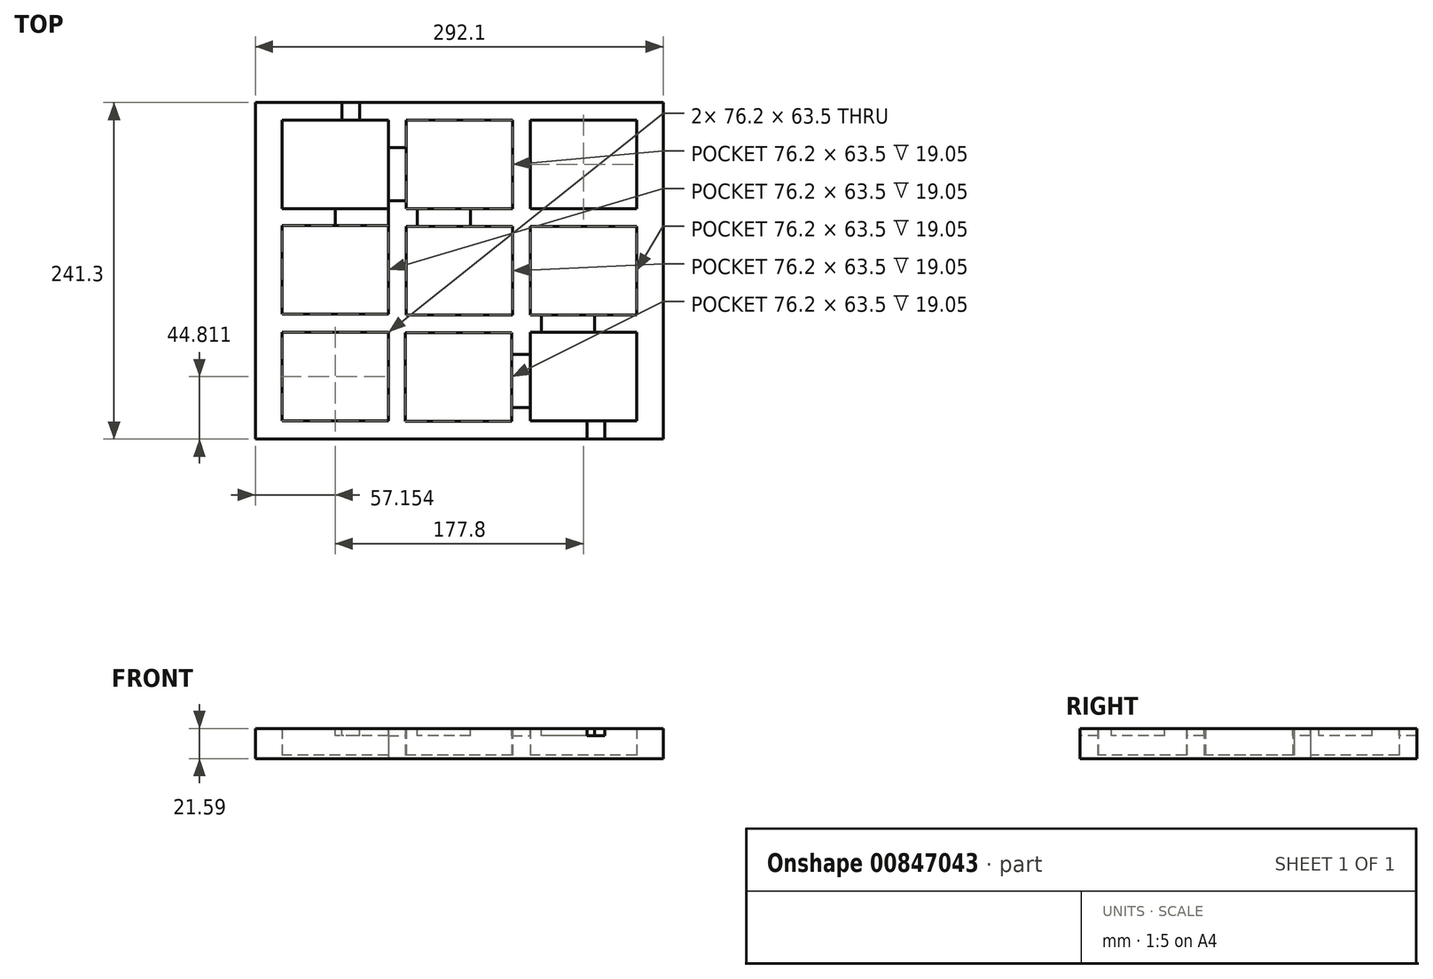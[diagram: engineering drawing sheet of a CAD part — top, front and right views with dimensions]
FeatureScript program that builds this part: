
annotation { "Feature Type Name" : "Feature", "Feature Type Description" : "" }
export const myFeature = defineFeature(function(context is Context, id is Id, definition is map)
    precondition{}
    {
        {
            var Q0;
            Q0=qCreatedBy(makeId("Top.planeOp"),FACE);
            var sketch = newSketch(context, id + "F0", { "sketchPlane" : qUnion([Q0])});
            skLineSegment(sketch, "E0.bottom", {"start": v(141.22, 122.08) * mm, "end": v(-150.88, 122.08) * mm});
            skLineSegment(sketch, "E0.top", {"start": v(141.22, -119.22) * mm, "end": v(-150.88, -119.22) * mm});
            skLineSegment(sketch, "E0.left", {"start": v(141.22, 122.08) * mm, "end": v(141.22, -119.22) * mm});
            skLineSegment(sketch, "E0.right", {"start": v(-150.88, 122.08) * mm, "end": v(-150.88, -119.22) * mm});
            skPoint(sketch, "E0.middle", {"position": v(-4.83, 77.63) * mm});
            skLineSegment(sketch, "E1.bottom", {"start": v(33.27, 109.38) * mm, "end": v(-42.93, 109.38) * mm});
            skLineSegment(sketch, "E1.top", {"start": v(33.27, 45.88) * mm, "end": v(-42.93, 45.88) * mm});
            skLineSegment(sketch, "E1.left", {"start": v(33.27, 109.38) * mm, "end": v(33.27, 45.88) * mm});
            skLineSegment(sketch, "E1.right", {"start": v(-42.93, 109.38) * mm, "end": v(-42.93, 45.88) * mm});
            skPoint(sketch, "E2.middle", {"position": v(-93.73, 2.2) * mm});
            skLineSegment(sketch, "E3.bottom", {"start": v(-55.63, 33.96) * mm, "end": v(-131.83, 33.96) * mm});
            skLineSegment(sketch, "E3.top", {"start": v(-55.63, -29.54) * mm, "end": v(-131.83, -29.54) * mm});
            skLineSegment(sketch, "E3.left", {"start": v(-55.63, 33.96) * mm, "end": v(-55.63, -29.54) * mm});
            skLineSegment(sketch, "E3.right", {"start": v(-131.83, 33.96) * mm, "end": v(-131.83, -29.54) * mm});
            skPoint(sketch, "E4.middle", {"position": v(84.07, 1.43) * mm});
            skLineSegment(sketch, "E5.bottom", {"start": v(122.17, 33.18) * mm, "end": v(45.97, 33.18) * mm});
            skLineSegment(sketch, "E5.top", {"start": v(122.17, -30.32) * mm, "end": v(45.97, -30.32) * mm});
            skLineSegment(sketch, "E5.left", {"start": v(122.17, 33.18) * mm, "end": v(122.17, -30.32) * mm});
            skLineSegment(sketch, "E5.right", {"start": v(45.97, 33.18) * mm, "end": v(45.97, -30.32) * mm});
            skPoint(sketch, "E6.middle", {"position": v(-4.83, 1.43) * mm});
            skLineSegment(sketch, "E7.bottom", {"start": v(33.27, 33.18) * mm, "end": v(-42.93, 33.18) * mm});
            skLineSegment(sketch, "E7.top", {"start": v(33.27, -30.32) * mm, "end": v(-42.93, -30.32) * mm});
            skLineSegment(sketch, "E7.left", {"start": v(33.27, 33.18) * mm, "end": v(33.27, -30.32) * mm});
            skLineSegment(sketch, "E7.right", {"start": v(-42.93, 33.18) * mm, "end": v(-42.93, -30.32) * mm});
            skPoint(sketch, "E8.middle", {"position": v(-5.2, -74.77) * mm});
            skLineSegment(sketch, "E9.bottom", {"start": v(32.9, -43.02) * mm, "end": v(-43.3, -43.02) * mm});
            skLineSegment(sketch, "E9.top", {"start": v(32.9, -106.52) * mm, "end": v(-43.3, -106.52) * mm});
            skLineSegment(sketch, "E9.left", {"start": v(32.9, -43.02) * mm, "end": v(32.9, -106.52) * mm});
            skLineSegment(sketch, "E9.right", {"start": v(-43.3, -43.02) * mm, "end": v(-43.3, -106.52) * mm});
            skLineSegment(sketch, "E10", {"start": v(-55.63, 9.6) * mm, "end": v(-42.93, 9.6) * mm});
            skPoint(sketch, "E11.middle", {"position": v(-93.73, 77.63) * mm});
            skLineSegment(sketch, "E12.bottom", {"start": v(-55.63, 109.38) * mm, "end": v(-131.83, 109.38) * mm});
            skLineSegment(sketch, "E12.top", {"start": v(-55.63, 45.88) * mm, "end": v(-131.83, 45.88) * mm});
            skLineSegment(sketch, "E12.left", {"start": v(-55.63, 109.38) * mm, "end": v(-55.63, 45.88) * mm});
            skLineSegment(sketch, "E12.right", {"start": v(-131.83, 109.38) * mm, "end": v(-131.83, 45.88) * mm});
            skPoint(sketch, "E13.middle", {"position": v(84.07, 77.63) * mm});
            skLineSegment(sketch, "E14.bottom", {"start": v(122.17, 109.38) * mm, "end": v(45.97, 109.38) * mm});
            skLineSegment(sketch, "E14.top", {"start": v(122.17, 45.88) * mm, "end": v(45.97, 45.88) * mm});
            skLineSegment(sketch, "E14.left", {"start": v(122.17, 109.38) * mm, "end": v(122.17, 45.88) * mm});
            skLineSegment(sketch, "E14.right", {"start": v(45.97, 109.38) * mm, "end": v(45.97, 45.88) * mm});
            skPoint(sketch, "E15.middle", {"position": v(84.07, -74.4) * mm});
            skLineSegment(sketch, "E16.bottom", {"start": v(122.17, -42.66) * mm, "end": v(45.97, -42.66) * mm});
            skLineSegment(sketch, "E16.top", {"start": v(122.17, -106.16) * mm, "end": v(45.97, -106.16) * mm});
            skLineSegment(sketch, "E16.left", {"start": v(122.17, -42.66) * mm, "end": v(122.17, -106.16) * mm});
            skLineSegment(sketch, "E16.right", {"start": v(45.97, -42.66) * mm, "end": v(45.97, -106.16) * mm});
            skPoint(sketch, "E17.middle", {"position": v(-93.73, -74.4) * mm});
            skLineSegment(sketch, "E18.bottom", {"start": v(-55.63, -42.66) * mm, "end": v(-131.83, -42.66) * mm});
            skLineSegment(sketch, "E18.top", {"start": v(-55.63, -106.16) * mm, "end": v(-131.83, -106.16) * mm});
            skLineSegment(sketch, "E18.left", {"start": v(-55.63, -42.66) * mm, "end": v(-55.63, -106.16) * mm});
            skLineSegment(sketch, "E18.right", {"start": v(-131.83, -42.66) * mm, "end": v(-131.83, -106.16) * mm});
            skSolve(sketch);
        }
        {
            var Q0;
            Q0=makeQuery(id+"F0.imprint","IMPRINT",FACE,{"disambiguationData":[TD([[makeQuery(id+"F0.imprint","IMPRINT",EDGE,{"derivedFrom":sQuery(id+"F0.wireOp",EDGE,"E0.bottom")}),1.0]])]});
            extrude(context, id + "F1", {"entities" : qUnion([Q0]), "depth" : 21.59 * mm, "offsetDistance" : 25.4 * mm});
        }
        {
            var Q0;
            Q0=makeQuery(id+"F0.imprint","IMPRINT",FACE,{"disambiguationData":[TD([[makeQuery(id+"F0.imprint","IMPRINT",EDGE,{"derivedFrom":sQuery(id+"F0.wireOp",EDGE,"E1.bottom")}),1.0]])]});
            var Q1;
            {var subQ1=sQuery(id+"F0.wireOp",EDGE,"E7.bottom");Q1=makeQuery(id+"F0.imprint","IMPRINT",FACE,{"disambiguationData":[TD([[makeQuery(id+"F0.imprint","IMPRINT",EDGE,{"derivedFrom":subQ1}),1.0]])]});}
            var Q2;
            Q2=makeQuery(id+"F0.imprint","IMPRINT",FACE,{"disambiguationData":[TD([[makeQuery(id+"F0.imprint","IMPRINT",EDGE,{"derivedFrom":sQuery(id+"F0.wireOp",EDGE,"E9.bottom")}),1.0]])]});
            var Q3;
            {var subQ3=sQuery(id+"F0.wireOp",EDGE,"E3.bottom");Q3=makeQuery(id+"F0.imprint","IMPRINT",FACE,{"disambiguationData":[TD([[makeQuery(id+"F0.imprint","IMPRINT",EDGE,{"derivedFrom":subQ3}),1.0]])]});}
            var Q4;
            Q4=makeQuery(id+"F0.imprint","IMPRINT",FACE,{"disambiguationData":[TD([[makeQuery(id+"F0.imprint","IMPRINT",EDGE,{"derivedFrom":sQuery(id+"F0.wireOp",EDGE,"E5.bottom")}),1.0]])]});
            extrude(context, id + "F2", {"entities" : qUnion([Q0, Q1, Q2, Q3, Q4]), "operationType" : NewBodyOperationType.ADD, "depth" : 2.54 * mm, "offsetDistance" : 25.4 * mm});
        }
        {
            var Q0;
            Q0=makeQuery(id+"F1.opExtrude","CAP_FACE",FACE,{"disambiguationData":[OSD([sQuery(id+"F0.wireOp",EDGE,"E0.bottom"),sQuery(id+"F0.wireOp",EDGE,"E0.top"),sQuery(id+"F0.wireOp",EDGE,"E0.left"),sQuery(id+"F0.wireOp",EDGE,"E0.right"),sQuery(id+"F0.wireOp",EDGE,"E1.bottom"),sQuery(id+"F0.wireOp",EDGE,"E1.top"),sQuery(id+"F0.wireOp",EDGE,"E1.left"),sQuery(id+"F0.wireOp",EDGE,"E1.right"),sQuery(id+"F0.wireOp",EDGE,"E3.bottom"),sQuery(id+"F0.wireOp",EDGE,"E3.top"),sQuery(id+"F0.wireOp",EDGE,"E3.left"),sQuery(id+"F0.wireOp",EDGE,"E3.right"),sQuery(id+"F0.wireOp",EDGE,"E5.bottom"),sQuery(id+"F0.wireOp",EDGE,"E5.top"),sQuery(id+"F0.wireOp",EDGE,"E5.left"),sQuery(id+"F0.wireOp",EDGE,"E5.right"),sQuery(id+"F0.wireOp",EDGE,"E7.bottom"),sQuery(id+"F0.wireOp",EDGE,"E7.top"),sQuery(id+"F0.wireOp",EDGE,"E7.left"),sQuery(id+"F0.wireOp",EDGE,"E7.right"),sQuery(id+"F0.wireOp",EDGE,"E9.bottom"),sQuery(id+"F0.wireOp",EDGE,"E9.top"),sQuery(id+"F0.wireOp",EDGE,"E9.left"),sQuery(id+"F0.wireOp",EDGE,"E9.right"),sQuery(id+"F0.wireOp",EDGE,"E12.bottom"),sQuery(id+"F0.wireOp",EDGE,"E12.top"),sQuery(id+"F0.wireOp",EDGE,"E12.left"),sQuery(id+"F0.wireOp",EDGE,"E12.right"),sQuery(id+"F0.wireOp",EDGE,"E14.bottom"),sQuery(id+"F0.wireOp",EDGE,"E14.top"),sQuery(id+"F0.wireOp",EDGE,"E14.left"),sQuery(id+"F0.wireOp",EDGE,"E14.right"),sQuery(id+"F0.wireOp",EDGE,"E16.bottom"),sQuery(id+"F0.wireOp",EDGE,"E16.top"),sQuery(id+"F0.wireOp",EDGE,"E16.left"),sQuery(id+"F0.wireOp",EDGE,"E16.right"),sQuery(id+"F0.wireOp",EDGE,"E18.bottom"),sQuery(id+"F0.wireOp",EDGE,"E18.top"),sQuery(id+"F0.wireOp",EDGE,"E18.left"),sQuery(id+"F0.wireOp",EDGE,"E18.right")])],"isStart":false});
            var sketch = newSketch(context, id + "F3", { "sketchPlane" : qUnion([Q0])});
            skLineSegment(sketch, "E19.bottom", {"start": v(-93.69, 45.88) * mm, "end": v(-55.59, 45.88) * mm});
            skLineSegment(sketch, "E19.top", {"start": v(-93.69, 33.96) * mm, "end": v(-55.59, 33.96) * mm});
            skLineSegment(sketch, "E19.left", {"start": v(-93.69, 45.88) * mm, "end": v(-93.69, 33.96) * mm});
            skLineSegment(sketch, "E19.right", {"start": v(-55.59, 45.88) * mm, "end": v(-55.59, 33.96) * mm});
            skLineSegment(sketch, "E20.bottom", {"start": v(-55.63, 89.88) * mm, "end": v(-42.93, 89.88) * mm});
            skLineSegment(sketch, "E20.top", {"start": v(-55.63, 51.78) * mm, "end": v(-42.93, 51.78) * mm});
            skLineSegment(sketch, "E20.left", {"start": v(-55.63, 89.88) * mm, "end": v(-55.63, 51.78) * mm});
            skLineSegment(sketch, "E20.right", {"start": v(-42.93, 89.88) * mm, "end": v(-42.93, 51.78) * mm});
            skLineSegment(sketch, "E21.bottom", {"start": v(-34.82, 45.88) * mm, "end": v(3.28, 45.88) * mm});
            skLineSegment(sketch, "E21.top", {"start": v(-34.82, 33.18) * mm, "end": v(3.28, 33.18) * mm});
            skLineSegment(sketch, "E21.left", {"start": v(-34.82, 45.88) * mm, "end": v(-34.82, 33.18) * mm});
            skLineSegment(sketch, "E21.right", {"start": v(3.28, 45.88) * mm, "end": v(3.28, 33.18) * mm});
            skLineSegment(sketch, "E22.bottom", {"start": v(-88.7, 122.08) * mm, "end": v(-76, 122.08) * mm});
            skLineSegment(sketch, "E22.top", {"start": v(-88.7, 109.38) * mm, "end": v(-76, 109.38) * mm});
            skLineSegment(sketch, "E22.left", {"start": v(-88.7, 122.08) * mm, "end": v(-88.7, 109.38) * mm});
            skLineSegment(sketch, "E22.right", {"start": v(-76, 122.08) * mm, "end": v(-76, 109.38) * mm});
            skLineSegment(sketch, "E23.bottom", {"start": v(86.61, -106.16) * mm, "end": v(99.31, -106.16) * mm});
            skLineSegment(sketch, "E23.top", {"start": v(86.61, -119.22) * mm, "end": v(99.31, -119.22) * mm});
            skLineSegment(sketch, "E23.left", {"start": v(86.61, -106.16) * mm, "end": v(86.61, -119.22) * mm});
            skLineSegment(sketch, "E23.right", {"start": v(99.31, -106.16) * mm, "end": v(99.31, -119.22) * mm});
            skLineSegment(sketch, "E24.bottom", {"start": v(54.14, -30.32) * mm, "end": v(92.24, -30.32) * mm});
            skLineSegment(sketch, "E24.top", {"start": v(54.14, -42.66) * mm, "end": v(92.24, -42.66) * mm});
            skLineSegment(sketch, "E24.left", {"start": v(54.14, -30.32) * mm, "end": v(54.14, -42.66) * mm});
            skLineSegment(sketch, "E24.right", {"start": v(92.24, -30.32) * mm, "end": v(92.24, -42.66) * mm});
            skLineSegment(sketch, "E25.bottom", {"start": v(32.9, -58.65) * mm, "end": v(45.97, -58.65) * mm});
            skLineSegment(sketch, "E25.top", {"start": v(32.9, -96.75) * mm, "end": v(45.97, -96.75) * mm});
            skLineSegment(sketch, "E25.left", {"start": v(32.9, -58.65) * mm, "end": v(32.9, -96.75) * mm});
            skLineSegment(sketch, "E25.right", {"start": v(45.97, -58.65) * mm, "end": v(45.97, -96.75) * mm});
            skSolve(sketch);
        }
        {
            var Q0;
            Q0=qSketchRegion(id+"F3",true);
            extrude(context, id + "F4", {"entities" : qUnion([Q0]), "operationType" : NewBodyOperationType.REMOVE, "oppositeDirection" : true, "depth" : 5.08 * mm, "offsetDistance" : 25.4 * mm});
        }
    });
